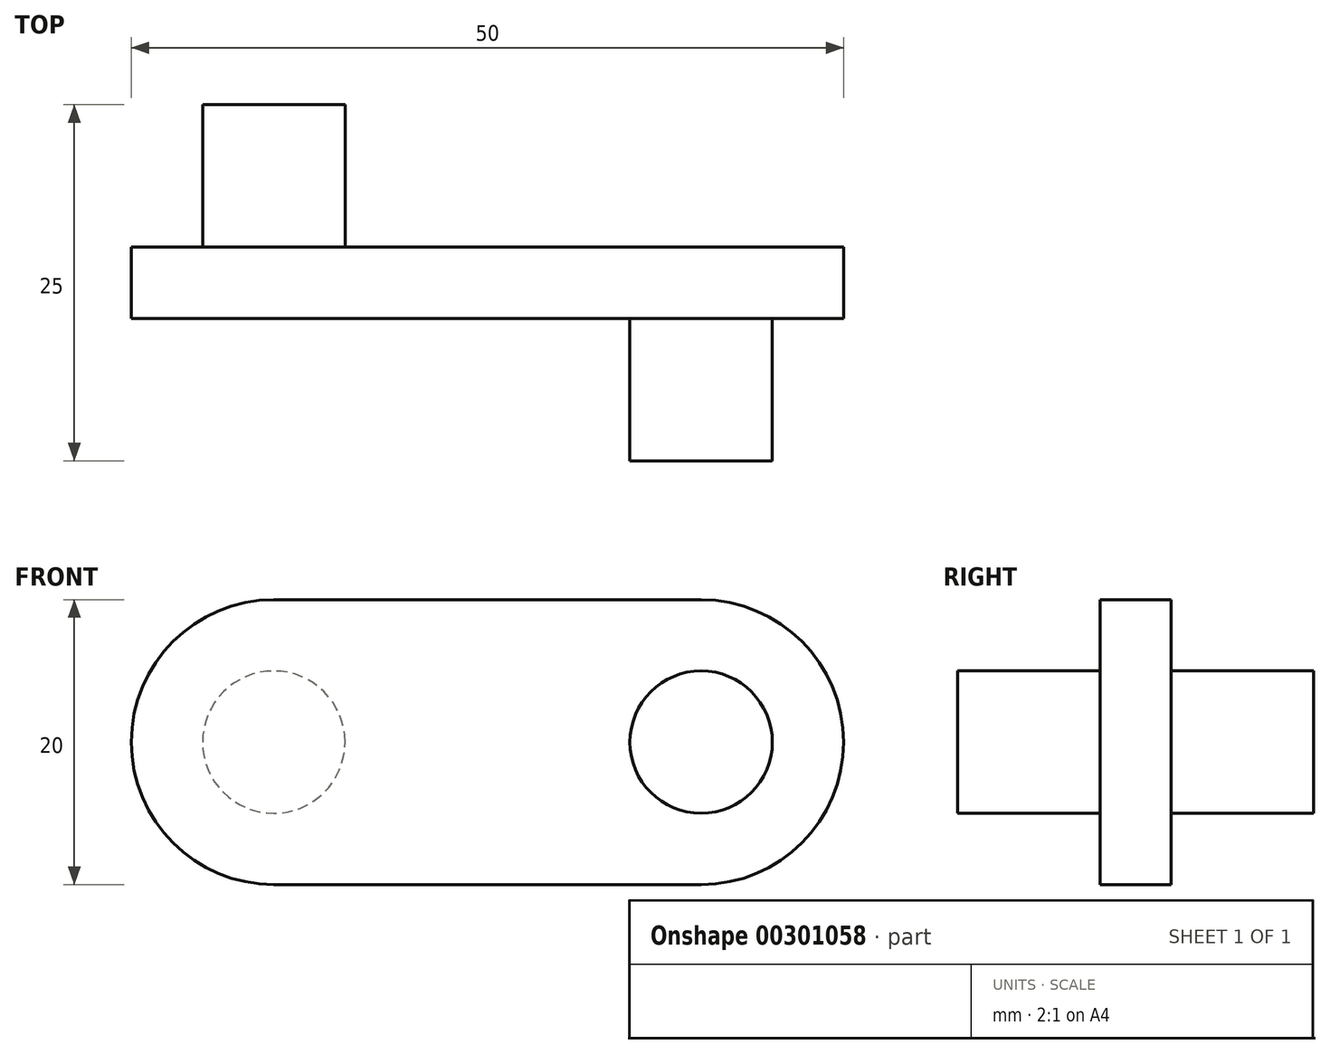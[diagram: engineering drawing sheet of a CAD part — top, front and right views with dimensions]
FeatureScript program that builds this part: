
annotation { "Feature Type Name" : "Feature", "Feature Type Description" : "" }
export const myFeature = defineFeature(function(context is Context, id is Id, definition is map)
    precondition{}
    {
        {
            var Q0;
            Q0=qCreatedBy(makeId("Front.planeOp"),FACE);
            var sketch = newSketch(context, id + "F0", { "sketchPlane" : qUnion([Q0])});
            skLineSegment(sketch, "E0", {"start": v(0, 10) * mm, "end": v(30, 10) * mm});
            skLineSegment(sketch, "E1", {"start": v(0, -10) * mm, "end": v(30, -10) * mm});
            skArc(sketch, "E2", {"start": v(0, -10) * mm, "mid": v(-10, 0) * mm, "end": v(0, 10) * mm});
            skArc(sketch, "E3", {"start": v(30, 10) * mm, "mid": v(40, 0) * mm, "end": v(30, -10) * mm});
            skCircle(sketch, "E4", {"center": v(0, 0) * mm, "radius": 5 * mm});
            skCircle(sketch, "E5", {"center": v(30, 0) * mm, "radius": 5 * mm});
            skSolve(sketch);
        }
        {
            var Q0;
            Q0=makeQuery(id+"F0.imprint","IMPRINT",FACE,{"disambiguationData":[TD([[makeQuery(id+"F0.imprint","IMPRINT",EDGE,{"derivedFrom":sQuery(id+"F0.wireOp",EDGE,"E0")}),-1.0]])]});
            extrude(context, id + "F1", {"entities" : qUnion([Q0]), "depth" : 5 * mm});
        }
        {
            var Q0;
            Q0=qCreatedBy(makeId("Front.planeOp"),FACE);
            var sketch = newSketch(context, id + "F2", { "sketchPlane" : qUnion([Q0])});
            skCircle(sketch, "E6", {"center": v(30, 0) * mm, "radius": 5 * mm});
            skSolve(sketch);
        }
        {
            var Q0;
            Q0 = qSketchRegion(id + "F2", true);
            extrude(context, id + "F3", {"entities" : qUnion([Q0]), "operationType" : NewBodyOperationType.ADD, "depth" : 15 * mm});
        }
        {
            var Q0;
            Q0=makeQuery(id+"F0.imprint","IMPRINT",FACE,{"disambiguationData":[TD([[makeQuery(id+"F0.imprint","IMPRINT",EDGE,{"derivedFrom":sQuery(id+"F0.wireOp",EDGE,"E4")}),1.0]])]});
            extrude(context, id + "F4", {"entities" : qUnion([Q0]), "operationType" : NewBodyOperationType.ADD, "endBound" : BoundingType.SYMMETRIC, "oppositeDirection" : true, "depth" : 20 * mm});
        }
        {
            var Q0;
            Q0=makeQuery(id+"F4.opExtrude","CAP_FACE",FACE,{"disambiguationData":[OSD([sQuery(id+"F0.wireOp",EDGE,"E4")])],"isStart":true});
            extrude(context, id + "F5", {"entities" : qUnion([Q0]), "operationType" : NewBodyOperationType.REMOVE, "oppositeDirection" : true, "depth" : 5 * mm});
        }
    });
